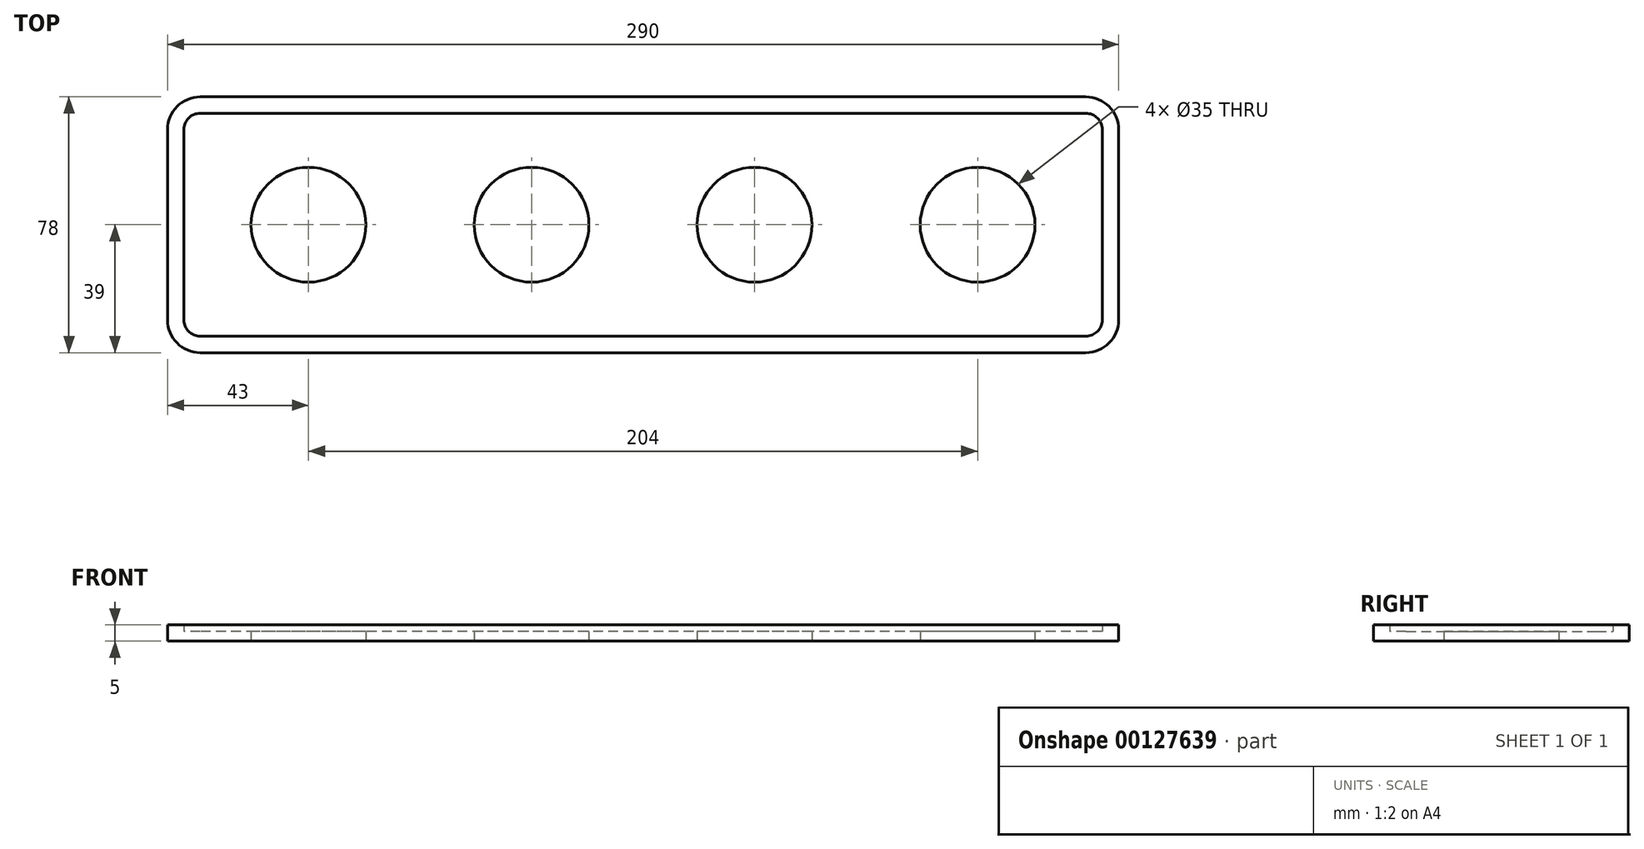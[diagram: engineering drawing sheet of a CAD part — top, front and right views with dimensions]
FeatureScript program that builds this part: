
annotation { "Feature Type Name" : "Feature", "Feature Type Description" : "" }
export const myFeature = defineFeature(function(context is Context, id is Id, definition is map)
    precondition{}
    {
        {
            var Q0;
            Q0=qCreatedBy(makeId("Top.planeOp"),FACE);
            var sketch = newSketch(context, id + "F0", { "sketchPlane" : qUnion([Q0])});
            skLineSegment(sketch, "E0.bottom", {"start": v(135, -34) * mm, "end": v(-135, -34) * mm});
            skLineSegment(sketch, "E0.top", {"start": v(135, 34) * mm, "end": v(-135, 34) * mm});
            skLineSegment(sketch, "E0.left", {"start": v(140, -29) * mm, "end": v(140, 0) * mm});
            skLineSegment(sketch, "E0.right", {"start": v(-140, -29) * mm, "end": v(-140, 29) * mm});
            skPoint(sketch, "E0.middle", {"position": v(0, 0) * mm});
            skLineSegment(sketch, "E1", {"start": v(0, 0) * mm, "end": v(186.51, 0) * mm, "construction": true});
            skLineSegment(sketch, "E2", {"start": v(0, 0) * mm, "end": v(-183.86, 0) * mm, "construction": true});
            skLineSegment(sketch, "E3", {"start": v(0, -34) * mm, "end": v(0, 34) * mm, "construction": true});
            skLineSegment(sketch, "E4.0", {"start": v(-68, -64.57) * mm, "end": v(-68, 64.57) * mm, "construction": true});
            skLineSegment(sketch, "E5.0", {"start": v(68, -64.57) * mm, "end": v(68, 64.57) * mm, "construction": true});
            skLineSegment(sketch, "E6.0", {"start": v(-34, -64.57) * mm, "end": v(-34, 64.57) * mm, "construction": true});
            skLineSegment(sketch, "E7.0", {"start": v(34, -64.57) * mm, "end": v(34, 64.57) * mm, "construction": true});
            skCircle(sketch, "E8", {"center": v(34, 0) * mm, "radius": 17.5 * mm});
            skCircle(sketch, "E9", {"center": v(-34, 0) * mm, "radius": 17.5 * mm});
            skLineSegment(sketch, "E10.0", {"start": v(-102, -64.57) * mm, "end": v(-102, 64.57) * mm, "construction": true});
            skLineSegment(sketch, "E11.0", {"start": v(102, -64.57) * mm, "end": v(102, 64.57) * mm, "construction": true});
            skCircle(sketch, "E12", {"center": v(-102, 0) * mm, "radius": 17.5 * mm});
            skCircle(sketch, "E13", {"center": v(102, 0) * mm, "radius": 17.5 * mm});
            skLineSegment(sketch, "E14", {"start": v(140, 0) * mm, "end": v(140, 29) * mm});
            skPoint(sketch, "E15.visualSharp", {"position": v(140, 34) * mm});
            skArc(sketch, "E15.filletArc", {"start": v(140, 29) * mm, "mid": v(138.54, 32.54) * mm, "end": v(135, 34) * mm});
            skPoint(sketch, "E16.visualSharp", {"position": v(140, -34) * mm});
            skArc(sketch, "E16.filletArc", {"start": v(135, -34) * mm, "mid": v(138.54, -32.54) * mm, "end": v(140, -29) * mm});
            skPoint(sketch, "E17.visualSharp", {"position": v(-140, 34) * mm});
            skArc(sketch, "E17.filletArc", {"start": v(-135, 34) * mm, "mid": v(-138.54, 32.54) * mm, "end": v(-140, 29) * mm});
            skPoint(sketch, "E18.visualSharp", {"position": v(-140, -34) * mm});
            skArc(sketch, "E18.filletArc", {"start": v(-140, -29) * mm, "mid": v(-138.54, -32.54) * mm, "end": v(-135, -34) * mm});
            skArc(sketch, "E19.0", {"start": v(135, -39) * mm, "mid": v(142.07, -36.07) * mm, "end": v(145, -29) * mm});
            skLineSegment(sketch, "E19.1", {"start": v(145, -29) * mm, "end": v(145, 0) * mm});
            skLineSegment(sketch, "E19.2", {"start": v(135, -39) * mm, "end": v(-135, -39) * mm});
            skLineSegment(sketch, "E19.3", {"start": v(145, 0) * mm, "end": v(145, 29) * mm});
            skArc(sketch, "E19.4", {"start": v(145, 29) * mm, "mid": v(142.07, 36.07) * mm, "end": v(135, 39) * mm});
            skArc(sketch, "E19.5", {"start": v(-145, -29) * mm, "mid": v(-142.07, -36.07) * mm, "end": v(-135, -39) * mm});
            skLineSegment(sketch, "E19.6", {"start": v(-145, -29) * mm, "end": v(-145, 29) * mm});
            skArc(sketch, "E19.7", {"start": v(-135, 39) * mm, "mid": v(-142.07, 36.07) * mm, "end": v(-145, 29) * mm});
            skLineSegment(sketch, "E19.8", {"start": v(135, 39) * mm, "end": v(-135, 39) * mm});
            skSolve(sketch);
        }
        {
            var Q0;
            Q0=makeQuery(id+"F0.imprint","IMPRINT",FACE,{"disambiguationData":[TD([[makeQuery(id+"F0.imprint","IMPRINT",EDGE,{"derivedFrom":sQuery(id+"F0.wireOp",EDGE,"E0.bottom")}),-1.0]])]});
            extrude(context, id + "F1", {"entities" : qUnion([Q0]), "depth" : 3 * mm});
        }
        {
            var Q0;
            Q0 = qSketchRegion(id + "F0", true);
            extrude(context, id + "F2", {"entities" : qUnion([Q0]), "operationType" : NewBodyOperationType.ADD, "depth" : 5 * mm});
        }
    });
